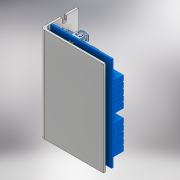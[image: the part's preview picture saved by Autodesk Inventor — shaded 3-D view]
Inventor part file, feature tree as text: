
AUTODESK INVENTOR PART (.ipt)
format: ipt  version: 2017 (Build 210142000, 142)  size: 5,351,936 bytes
history: native  units: mm
features: other x25, sketch x8, extrude x5, mirror x1, hole x1
ambient origin geometry x8: Origin, YZ Plane, XZ Plane, XY Plane, X Axis, Y Axis, Z Axis, Center Point
bodies: Solide1 (feature_tree), Solide2 (feature_tree), Solide3 (feature_tree), Solide4 (feature_tree), Solide5 (feature_tree), Solide6 (feature_tree), Solide7 (feature_tree), Solide8 (feature_tree), Solide9 (feature_tree)
feature tree (40):
  other  "Connecteur jst 6 broches.iam"
  other  "Connecteur jst 2 broches.iam"
  other  "Connecteur jst 4 broches.iam"
  other  "Connecteur jst 5 broches.iam"
  other  "Connecteur jst 3 broches.iam"
  other  "Connecteur jst 6 broches femelle.ipt:1"
  other  "Connecteur JST 6 Broches Male.ipt:1"
  other  "Connecteur jst 2 broches femelle.ipt:1"
  other  "Connecteur JST 2 Broches Male.ipt:1"
  other  "Connecteur jst 4 broches femelle.ipt:1"
  other  "Connecteur JST 4 Broches Male.ipt:1"
  other  "Connecteur jst 5 broches femelle.ipt:1"
  other  "Connecteur JST 5 Broches Male.ipt:1"
  other  "Connecteur jst 3 broches femelle.ipt:1"
  other  "Connecteur JST 3 Broches Male.ipt:1"
  extrude  "Extrusion1"  Depth=2.0mm
  extrude  "Extrusion2"  Depth=2.0mm
  mirror  "Symétrie1"
  extrude  "Extrusion3"  Depth=33.5mm
  extrude  "Extrusion4"  Depth=58.5mm
  other  "Décalcomanie1"
  extrude  "Extrusion5"  Depth=87.4mm TaperAngle=0.0deg
  hole  "Perçage1"  [1 undecoded]
  other  "Déplacer des corps1"
  other  "Déplacer des corps2"
  other  "Déplacer des corps3"
  other  "Déplacer des corps4"
  other  "Déplacer des corps5"
  other  "Déplacer des corps6"
  other  "Déplacer des corps7"
  other  "Combiner1"
  sketch  "Esquisse9"
  sketch  "Esquisse1"
  sketch  "Esquisse2"
  sketch  "Esquisse3"
  sketch  "Esquisse4"
  sketch  "Esquisse5"
  sketch  "Esquisse6"
  sketch  "Esquisse7"
  other  "Image1"
note: 1 required parameter value undecoded (feature->parameter linkage not recoverable at this tier; creation-order binding heuristic only, values carry confidence <= 0.55)
